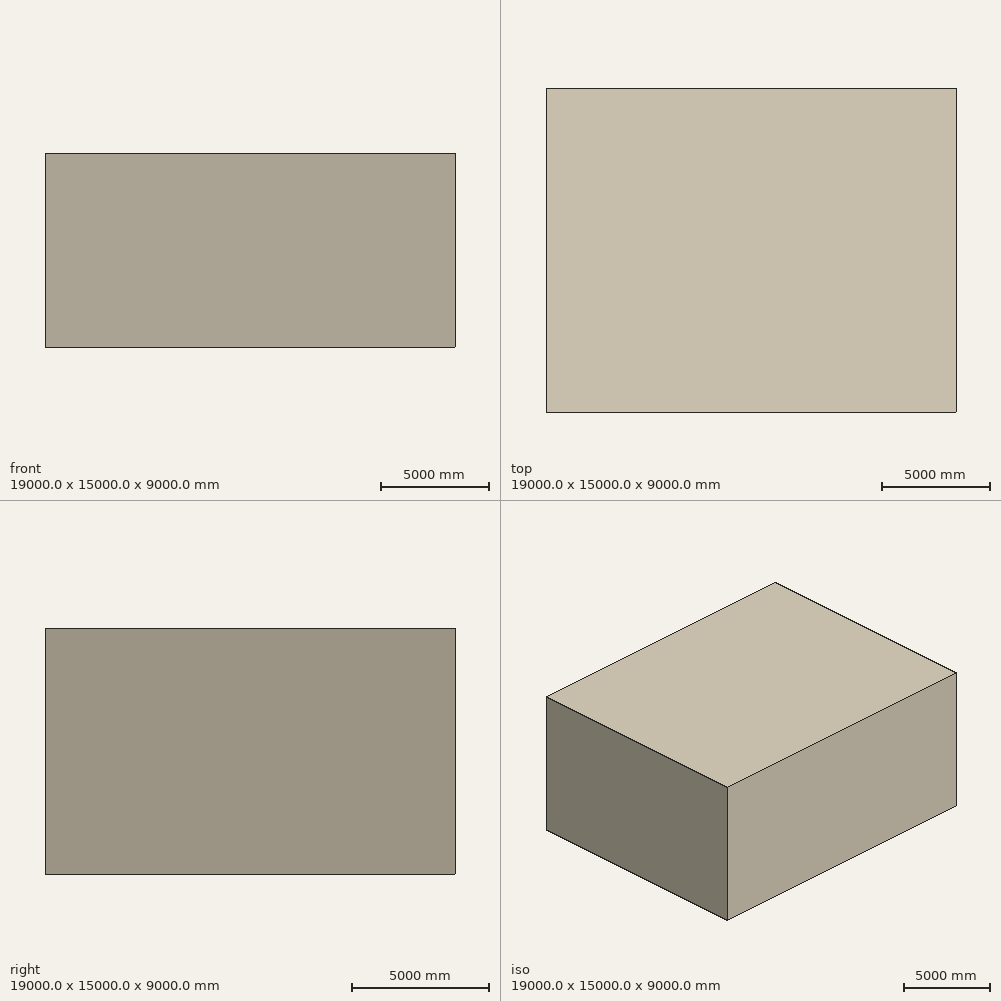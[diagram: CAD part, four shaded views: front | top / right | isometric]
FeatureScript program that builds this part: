
annotation { "Feature Type Name" : "Feature", "Feature Type Description" : "" }
export const myFeature = defineFeature(function(context is Context, id is Id, definition is map)
    precondition{}
    {
        {
            var Q0;
            Q0=qCreatedBy(makeId("Top.planeOp"),FACE);
            var sketch = newSketch(context, id + "F0", { "sketchPlane" : qUnion([Q0])});
            skLineSegment(sketch, "E0.bottom", {"start": v(0, 0) * mm, "end": v(19000, 0) * mm});
            skLineSegment(sketch, "E0.top", {"start": v(0, -15000) * mm, "end": v(19000, -15000) * mm});
            skLineSegment(sketch, "E0.left", {"start": v(0, 0) * mm, "end": v(0, -15000) * mm});
            skLineSegment(sketch, "E0.right", {"start": v(19000, 0) * mm, "end": v(19000, -15000) * mm});
            skSolve(sketch);
        }
        {
            var Q0;
            Q0=makeQuery(id+"F0.imprint","IMPRINT",FACE,{"disambiguationData":[TD([[makeQuery(id+"F0.imprint","IMPRINT",EDGE,{"derivedFrom":sQuery(id+"F0.wireOp",EDGE,"E0.bottom")}),-1.0]])]});
            extrude(context, id + "F1", {"entities" : qUnion([Q0]), "depth" : 9000 * mm});
        }
    });
